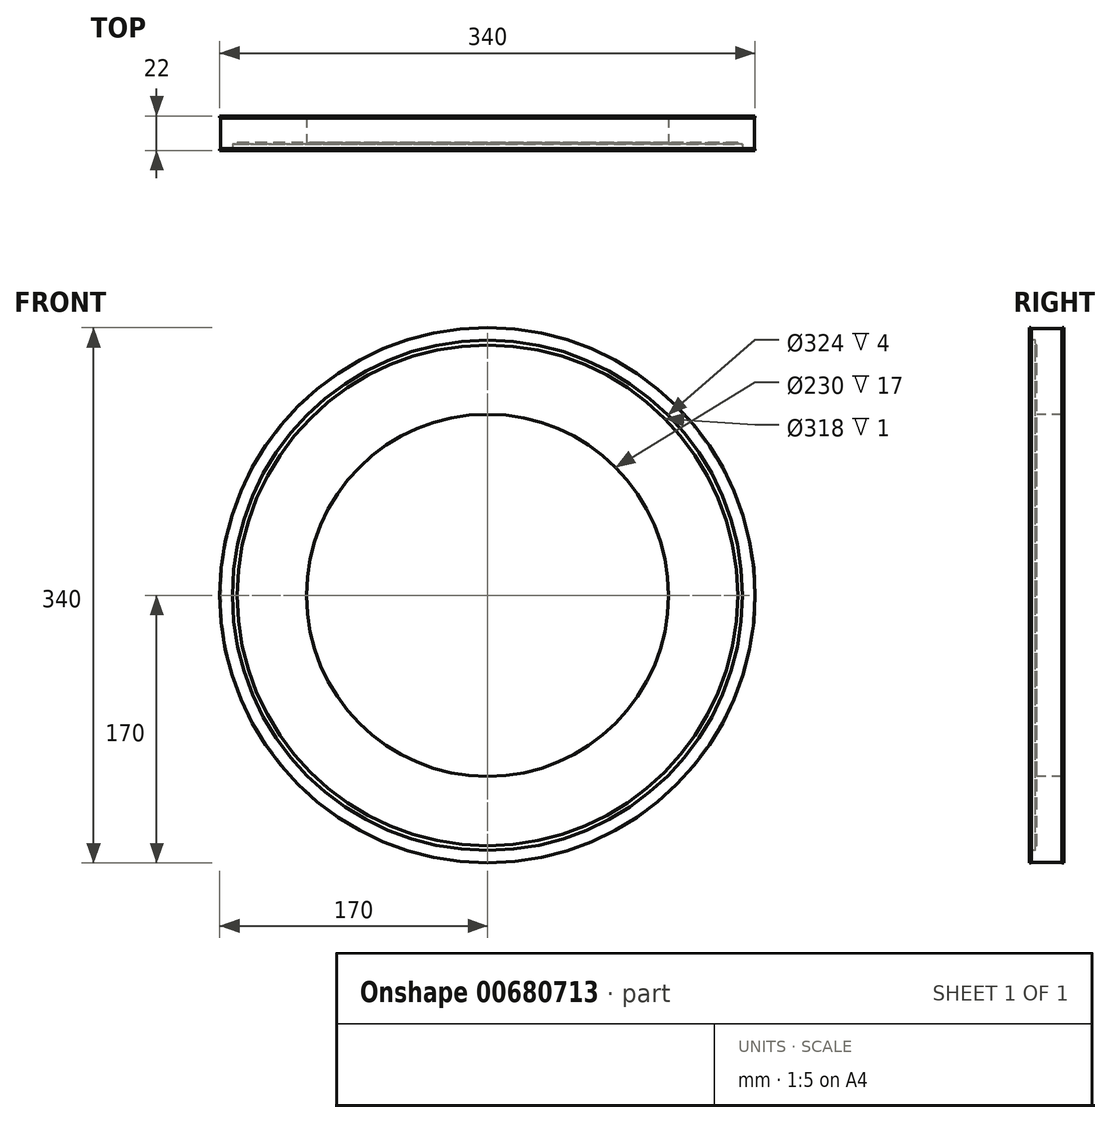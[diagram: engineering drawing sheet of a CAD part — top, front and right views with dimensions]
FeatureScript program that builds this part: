
annotation { "Feature Type Name" : "Feature", "Feature Type Description" : "" }
export const myFeature = defineFeature(function(context is Context, id is Id, definition is map)
    precondition{}
    {
        {
            var Q0;
            Q0=qCreatedBy(makeId("Top.planeOp"),FACE);
            var sketch = newSketch(context, id + "F0", { "sketchPlane" : qUnion([Q0])});
            skLineSegment(sketch, "E0", {"start": v(0, 0) * mm, "end": v(0, 22) * mm, "construction": true});
            skLineSegment(sketch, "E1", {"start": v(0, 22) * mm, "end": v(115, 22) * mm, "construction": true});
            skLineSegment(sketch, "E2", {"start": v(115, 22) * mm, "end": v(170, 22) * mm});
            skLineSegment(sketch, "E3", {"start": v(170, 22) * mm, "end": v(170, 21) * mm});
            skLineSegment(sketch, "E4", {"start": v(170, 0) * mm, "end": v(162, 0) * mm});
            skLineSegment(sketch, "E5", {"start": v(162, 0) * mm, "end": v(162, 4) * mm});
            skLineSegment(sketch, "E6", {"start": v(162, 4) * mm, "end": v(159, 4) * mm});
            skLineSegment(sketch, "E7", {"start": v(159, 4) * mm, "end": v(159, 5) * mm});
            skLineSegment(sketch, "E8", {"start": v(159, 5) * mm, "end": v(115, 5) * mm});
            skLineSegment(sketch, "E9", {"start": v(115, 5) * mm, "end": v(115, 22) * mm});
            skLineSegment(sketch, "E10", {"start": v(162, 0) * mm, "end": v(0, 0) * mm, "construction": true});
            skLineSegment(sketch, "E11", {"start": v(170, 21) * mm, "end": v(169.5, 20.77) * mm});
            skLineSegment(sketch, "E12", {"start": v(169.5, 20.77) * mm, "end": v(169.5, 1.23) * mm});
            skLineSegment(sketch, "E13", {"start": v(169.5, 1.23) * mm, "end": v(170, 1) * mm});
            skLineSegment(sketch, "E14.trimOffspring", {"start": v(170, 1) * mm, "end": v(170, 0) * mm});
            skSolve(sketch);
        }
        {
            var Q0;
            Q0 = qSketchRegion(id + "F0", true);
            var Q1;
            Q1=sQuery(id+"F0.wireOp",EDGE,"E0");
            revolve(context, id + "F1", {"entities" : qUnion([Q0]), "axis" : qUnion([Q1]), "revolveType" : RevolveType.FULL});
        }
    });
